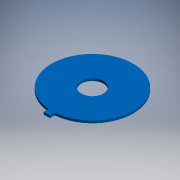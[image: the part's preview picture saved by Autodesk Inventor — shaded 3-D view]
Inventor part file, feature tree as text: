
AUTODESK INVENTOR PART (.ipt)
format: ipt  version: 2016 (Build 200138000, 138)  size: 123,392 bytes
history: native  units: mm (DEFAULTED — no unit token found)
features: extrude x1, sketch x1, other x1
ambient origin geometry x8: Origin, YZ Plane, XZ Plane, XY Plane, X Axis, Y Axis, Z Axis, Center Point
bodies: Solid1 (feature_tree)
feature tree (3):
  extrude  "Extrusion1"  Depth=0.3mm TaperAngle=0.0deg
  sketch  "Sketch1"  dims[d0=30.0mm d1=0.3mm d2=0.0mm]
  other  "24116-001-1-solid1"
